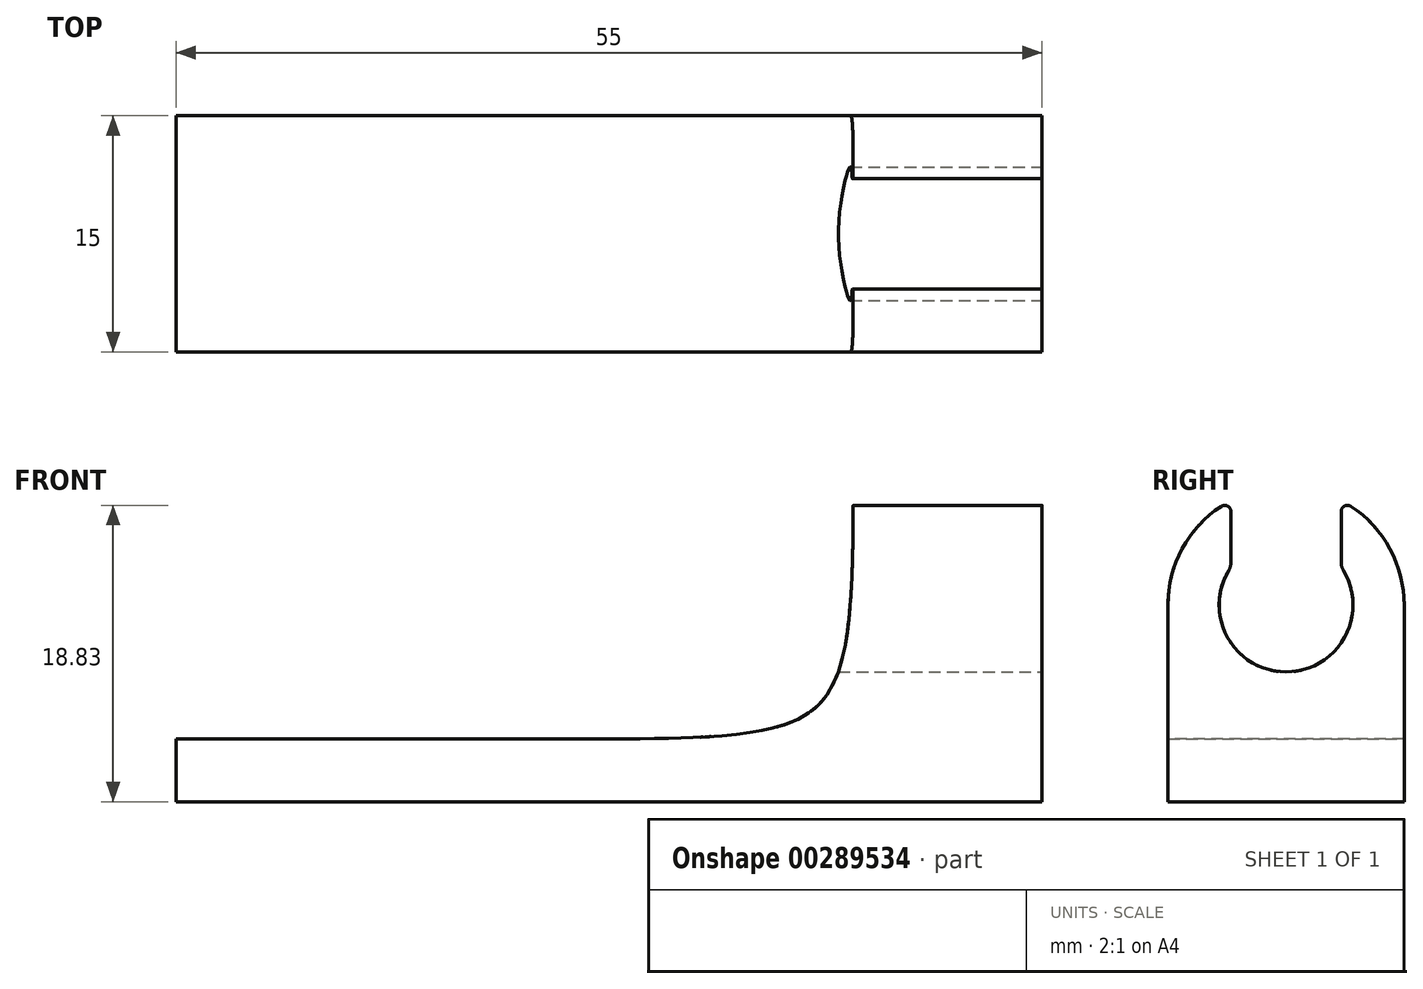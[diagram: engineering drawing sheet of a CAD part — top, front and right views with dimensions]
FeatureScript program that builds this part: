
annotation { "Feature Type Name" : "Feature", "Feature Type Description" : "" }
export const myFeature = defineFeature(function(context is Context, id is Id, definition is map)
    precondition{}
    {
        {
            var Q0;
            Q0=qCreatedBy(makeId("Top.planeOp"),FACE);
            var sketch = newSketch(context, id + "F0", { "sketchPlane" : qUnion([Q0])});
            skLineSegment(sketch, "E0.bottom", {"start": v(27.5, 7.5) * mm, "end": v(-27.5, 7.5) * mm});
            skLineSegment(sketch, "E0.top", {"start": v(27.5, -7.5) * mm, "end": v(-27.5, -7.5) * mm});
            skLineSegment(sketch, "E0.left", {"start": v(27.5, 7.5) * mm, "end": v(27.5, -7.5) * mm});
            skLineSegment(sketch, "E0.right", {"start": v(-27.5, 7.5) * mm, "end": v(-27.5, -7.5) * mm});
            skPoint(sketch, "E0.middle", {"position": v(0, 0) * mm});
            skSolve(sketch);
        }
        {
            var Q0;
            Q0=makeQuery(id+"F0.imprint","IMPRINT",FACE,{"disambiguationData":[TD([[makeQuery(id+"F0.imprint","IMPRINT",EDGE,{"derivedFrom":sQuery(id+"F0.wireOp",EDGE,"E0.bottom")}),1.0]])]});
            extrude(context, id + "F1", {"entities" : qUnion([Q0]), "depth" : 20 * mm});
        }
        {
            var Q0;
            Q0=makeQuery(id+"F1.opExtrude","SWEPT_FACE",FACE,{"disambiguationData":[OSD([sQuery(id+"F0.wireOp",EDGE,"E0.left")])]});
            var sketch = newSketch(context, id + "F2", { "sketchPlane" : qUnion([Q0])});
            skArc(sketch, "E1", {"start": v(7.5, 12.5) * mm, "mid": v(6.6, 16.06) * mm, "end": v(4.12, 18.77) * mm});
            skPoint(sketch, "E1.first.point", {"position": v(0, 20) * mm});
            skPoint(sketch, "E1.second.point", {"position": v(-7.5, 12.5) * mm});
            skPoint(sketch, "E1.third.point", {"position": v(7.5, 12.5) * mm});
            skLineSegment(sketch, "E2.left", {"start": v(-7.5, 20) * mm, "end": v(-7.5, 12.5) * mm});
            skLineSegment(sketch, "E2.right", {"start": v(7.5, 20) * mm, "end": v(7.5, 12.5) * mm});
            skArc(sketch, "E3", {"start": v(-3.64, 14.69) * mm, "mid": v(0, 8.25) * mm, "end": v(3.64, 14.69) * mm});
            skLineSegment(sketch, "E4.left", {"start": v(-3.5, 18.43) * mm, "end": v(-3.5, 15.2) * mm});
            skLineSegment(sketch, "E4.right", {"start": v(3.5, 18.43) * mm, "end": v(3.5, 15.2) * mm});
            skArc(sketch, "E5.trimOffspring", {"start": v(-4.12, 18.77) * mm, "mid": v(-6.6, 16.06) * mm, "end": v(-7.5, 12.5) * mm});
            skPoint(sketch, "E6.orphan", {"position": v(-3.5, 12.5) * mm});
            skPoint(sketch, "E7.orphan", {"position": v(3.5, 12.5) * mm});
            skLineSegment(sketch, "E8", {"start": v(-7.5, 20) * mm, "end": v(7.5, 20) * mm});
            skPoint(sketch, "E9.visualSharp", {"position": v(-3.5, 19.13) * mm});
            skArc(sketch, "E9.filletArc", {"start": v(-3.5, 18.43) * mm, "mid": v(-3.71, 18.79) * mm, "end": v(-4.12, 18.77) * mm});
            skPoint(sketch, "E10.visualSharp", {"position": v(3.5, 19.13) * mm});
            skArc(sketch, "E10.filletArc", {"start": v(4.12, 18.77) * mm, "mid": v(3.71, 18.79) * mm, "end": v(3.5, 18.43) * mm});
            skPoint(sketch, "E11.visualSharp", {"position": v(-3.5, 14.91) * mm});
            skArc(sketch, "E11.filletArc", {"start": v(-3.64, 14.69) * mm, "mid": v(-3.54, 14.94) * mm, "end": v(-3.5, 15.2) * mm});
            skPoint(sketch, "E12.visualSharp", {"position": v(3.5, 14.91) * mm});
            skArc(sketch, "E12.filletArc", {"start": v(3.5, 15.2) * mm, "mid": v(3.54, 14.94) * mm, "end": v(3.64, 14.69) * mm});
            skSolve(sketch);
        }
        {
            var Q0;
            Q0 = qSketchRegion(id + "F2", true);
            extrude(context, id + "F3", {"entities" : qUnion([Q0]), "operationType" : NewBodyOperationType.REMOVE, "endBound" : BoundingType.THROUGH_ALL, "oppositeDirection" : true, "depth" : 25 * mm});
        }
        {
            var Q0;
            Q0=makeQuery(id+"F1.opExtrude","SWEPT_FACE",FACE,{"disambiguationData":[OSD([sQuery(id+"F0.wireOp",EDGE,"E0.top")])]});
            var sketch = newSketch(context, id + "F4", { "sketchPlane" : qUnion([Q0])});
            skLineSegment(sketch, "E13", {"start": v(-27.5, 4) * mm, "end": v(15.5, 4) * mm});
            skLineSegment(sketch, "E14", {"start": v(15.5, 4) * mm, "end": v(15.5, 24) * mm});
            skLineSegment(sketch, "E15", {"start": v(15.5, 24) * mm, "end": v(-27.5, 24) * mm});
            skLineSegment(sketch, "E16", {"start": v(-27.5, 24) * mm, "end": v(-27.5, 4) * mm});
            skPoint(sketch, "E17.visualSharp", {"position": v(15.5, 4) * mm});
            skLineSegment(sketch, "E17.filletArc", {"start": v(15.5, 4) * mm, "end": v(15.5, 4) * mm});
            skSolve(sketch);
        }
        {
            var Q0;
            Q0 = qSketchRegion(id + "F4", true);
            extrude(context, id + "F5", {"entities" : qUnion([Q0]), "operationType" : NewBodyOperationType.REMOVE, "endBound" : BoundingType.THROUGH_ALL, "oppositeDirection" : true, "depth" : 25 * mm});
        }
        {
            var Q0;
            Q0=makeQuery(id+"F5.boolean.opBoolean","COPY",EDGE,{"derivedFrom":makeQuery(id+"F5.opExtrude","SWEPT_EDGE",EDGE,{"disambiguationData":[OSD([sQuery(id+"F4.wireOp",EDGE,"E13"),sQuery(id+"F4.wireOp",EDGE,"E14")])]})});
            fillet(context, id + "F6", {"entities" : qUnion([Q0]), "radius" : 14.5 * mm, "tangentPropagation" : true, "rho" : 0.7, "crossSection" : FilletCrossSection.CONIC, "allowEdgeOverflow" : false});
        }
    });
